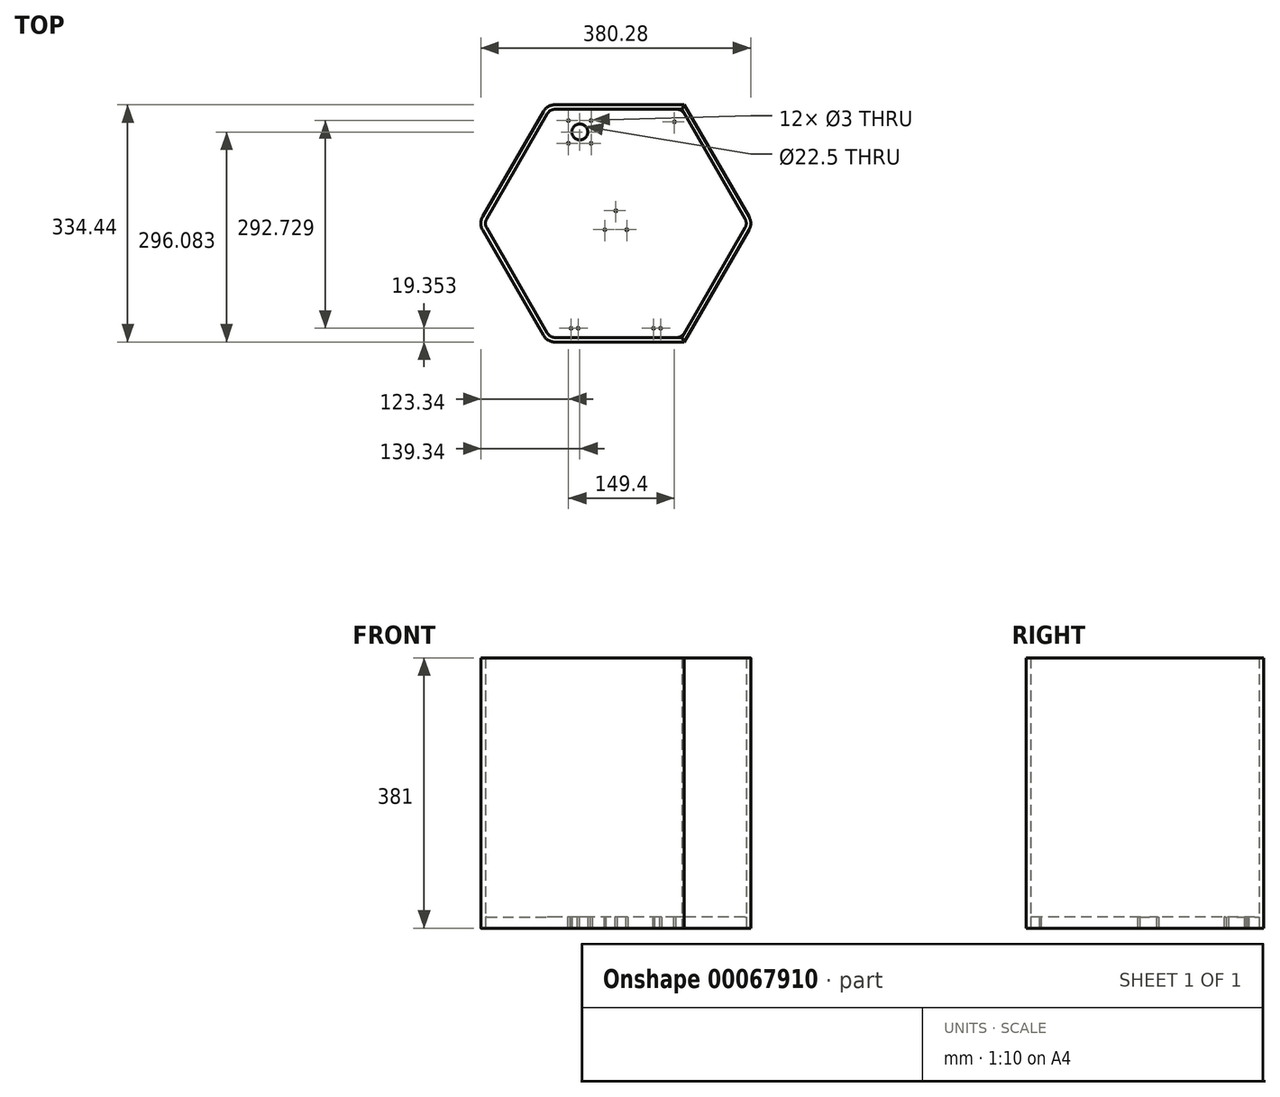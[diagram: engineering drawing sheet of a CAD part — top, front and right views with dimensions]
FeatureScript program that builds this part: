
annotation { "Feature Type Name" : "Feature", "Feature Type Description" : "" }
export const myFeature = defineFeature(function(context is Context, id is Id, definition is map)
    precondition{}
    {
        {
            var Q0;
            Q0=qCreatedBy(makeId("Top.planeOp"),FACE);
            var sketch = newSketch(context, id + "F0", { "sketchPlane" : qUnion([Q0])});
            skCircle(sketch, "E0.cCircle", {"center": v(0, 0) * mm, "radius": 160.87 * mm, "construction": true});
            skLineSegment(sketch, "E0.0", {"start": v(92.88, 160.87) * mm, "end": v(185.75, 0) * mm});
            skLineSegment(sketch, "E0.1", {"start": v(92.88, -160.87) * mm, "end": v(-92.88, -160.87) * mm});
            skLineSegment(sketch, "E0.2", {"start": v(-185.75, 0) * mm, "end": v(-92.88, 160.87) * mm});
            skPoint(sketch, "E0.0.midPoint", {"position": v(139.31, 80.43) * mm});
            skLineSegment(sketch, "E1.0", {"start": v(185.75, 0) * mm, "end": v(92.88, -160.87) * mm});
            skLineSegment(sketch, "E1.1", {"start": v(-92.88, -160.87) * mm, "end": v(-185.75, 0) * mm});
            skLineSegment(sketch, "E1.2", {"start": v(-92.88, 160.87) * mm, "end": v(92.88, 160.87) * mm});
            skPoint(sketch, "E1.0.midPoint", {"position": v(139.31, -80.43) * mm});
            skPoint(sketch, "E2.orphan", {"position": v(0, -321.73) * mm});
            skPoint(sketch, "E3.orphan", {"position": v(278.63, -160.87) * mm});
            skPoint(sketch, "E4.orphan", {"position": v(278.63, 160.87) * mm});
            skPoint(sketch, "E5.orphan", {"position": v(-278.63, 160.87) * mm});
            skPoint(sketch, "E6.orphan", {"position": v(-278.63, -160.87) * mm});
            skPoint(sketch, "E7.orphan", {"position": v(0, 321.73) * mm});
            skSolve(sketch);
        }
        {
            var Q0;
            Q0=makeQuery(id+"F0.imprint","IMPRINT",FACE,{"disambiguationData":[TD([[makeQuery(id+"F0.imprint","IMPRINT",EDGE,{"derivedFrom":sQuery(id+"F0.wireOp",EDGE,"E0.0")}),-1.0]])]});
            extrude(context, id + "F1", {"entities" : qUnion([Q0]), "depth" : 15.88 * mm});
        }
        {
            var Q0;
            Q0=makeQuery(id+"F1.opExtrude","SWEPT_EDGE",EDGE,{"disambiguationData":[OSD([sQuery(id+"F0.wireOp",EDGE,"E0.1"),sQuery(id+"F0.wireOp",EDGE,"E0.2")])]});
            var Q1;
            Q1=makeQuery(id+"F1.opExtrude","SWEPT_EDGE",EDGE,{"disambiguationData":[OSD([sQuery(id+"F0.wireOp",EDGE,"E0.0"),sQuery(id+"F0.wireOp",EDGE,"E0.1")])]});
            var Q2;
            Q2=makeQuery(id+"F1.opExtrude","SWEPT_EDGE",EDGE,{"disambiguationData":[OSD([sQuery(id+"F0.wireOp",EDGE,"E0.0"),sQuery(id+"F0.wireOp",EDGE,"E0.2")])]});
            fillet(context, id + "F2", {"entities" : qUnion([Q0, Q1, Q2]), "radius" : 12.7 * mm, "tangentPropagation" : true, "allowEdgeOverflow" : false});
        }
        {
            var Q0;
            Q0=qCreatedBy(makeId("Top.planeOp"),FACE);
            var sketch = newSketch(context, id + "F3", { "sketchPlane" : qUnion([Q0])});
            skPoint(sketch, "E8", {"position": v(-63.1, -147.87) * mm});
            skPoint(sketch, "E9", {"position": v(-53.1, -147.87) * mm});
            skPoint(sketch, "E10", {"position": v(53.1, -147.87) * mm});
            skPoint(sketch, "E11", {"position": v(63.1, -147.87) * mm});
            skSolve(sketch);
        }
        {
            var Q0;
            Q0=sQuery(id+"F3.wireOp",VERTEX,"E8");
            var Q1;
            Q1=sQuery(id+"F3.wireOp",VERTEX,"E9");
            var Q2;
            Q2=sQuery(id+"F3.wireOp",VERTEX,"E10");
            var Q3;
            Q3=sQuery(id+"F3.wireOp",VERTEX,"E11");
            var Q4;
            Q4=makeQuery(id+"F1.opExtrude","SWEPT_BODY",BODY,{"disambiguationData":[OSD([sQuery(id+"F0.wireOp",EDGE,"E0.0"),sQuery(id+"F0.wireOp",EDGE,"E0.1"),sQuery(id+"F0.wireOp",EDGE,"E0.2")])]});
            hole(context, id + "F4", {"style" : HoleStyle.SIMPLE, "endStyle" : HoleEndStyle.THROUGH, "oppositeDirection" : true, "holeDiameter" : 3 * mm, "locations" : qUnion([Q0, Q1, Q2, Q3]), "scope" : qUnion([Q4]), "isTappedThrough" : true});
        }
        {
            var Q0;
            Q0=qCreatedBy(makeId("Front.planeOp"),FACE);
            var sketch = newSketch(context, id + "F5", { "sketchPlane" : qUnion([Q0])});
            skLineSegment(sketch, "E12", {"start": v(0, 0) * mm, "end": v(0, 55.48) * mm});
            skSolve(sketch);
        }
        {
            var Q0;
            Q0=qCreatedBy(makeId("Top.planeOp"),FACE);
            var sketch = newSketch(context, id + "F6", { "sketchPlane" : qUnion([Q0])});
            skCircle(sketch, "E13.cCircle", {"center": v(0, 0) * mm, "radius": 8.89 * mm, "construction": true});
            skLineSegment(sketch, "E13.0", {"start": v(0, 17.78) * mm, "end": v(15.4, -8.9) * mm});
            skLineSegment(sketch, "E13.1", {"start": v(15.4, -8.9) * mm, "end": v(-15.4, -8.9) * mm});
            skLineSegment(sketch, "E13.2", {"start": v(-15.4, -8.89) * mm, "end": v(0, 17.78) * mm});
            skPoint(sketch, "E13.0.midPoint", {"position": v(7.7, 4.44) * mm});
            skSolve(sketch);
        }
        {
            var Q0;
            Q0=sQuery(id+"F6.wireOp",VERTEX,"E13.2.end");
            var Q1;
            Q1=sQuery(id+"F6.wireOp",VERTEX,"E13.1.end");
            var Q2;
            Q2=sQuery(id+"F6.wireOp",VERTEX,"E13.0.end");
            var Q3;
            Q3=makeQuery(id+"F1.opExtrude","SWEPT_BODY",BODY,{"disambiguationData":[OSD([sQuery(id+"F0.wireOp",EDGE,"E0.0"),sQuery(id+"F0.wireOp",EDGE,"E0.1"),sQuery(id+"F0.wireOp",EDGE,"E0.2")])]});
            hole(context, id + "F7", {"style" : HoleStyle.SIMPLE, "endStyle" : HoleEndStyle.THROUGH, "oppositeDirection" : true, "holeDiameter" : 3 * mm, "locations" : qUnion([Q0, Q1, Q2]), "scope" : qUnion([Q3]), "isTappedThrough" : true});
        }
        {
            var Q0;
            Q0=makeQuery(id+"F1.opExtrude","CAP_FACE",FACE,{"disambiguationData":[OSD([sQuery(id+"F0.wireOp",EDGE,"E0.0"),sQuery(id+"F0.wireOp",EDGE,"E0.1"),sQuery(id+"F0.wireOp",EDGE,"E0.2"),sQuery(id+"F0.wireOp",EDGE,"E1.0"),sQuery(id+"F0.wireOp",EDGE,"E1.1"),sQuery(id+"F0.wireOp",EDGE,"E1.2")])],"isStart":true});
            var sketch = newSketch(context, id + "F8", { "sketchPlane" : qUnion([Q0])});
            skLineSegment(sketch, "E14.bottom", {"start": v(-34.8, -112.86) * mm, "end": v(-66.8, -112.86) * mm});
            skLineSegment(sketch, "E14.top", {"start": v(-34.8, -144.86) * mm, "end": v(-66.8, -144.86) * mm});
            skLineSegment(sketch, "E14.left", {"start": v(-34.8, -112.86) * mm, "end": v(-34.8, -144.86) * mm});
            skLineSegment(sketch, "E14.right", {"start": v(-66.8, -112.86) * mm, "end": v(-66.8, -144.86) * mm});
            skPoint(sketch, "E14.middle", {"position": v(-50.8, -128.86) * mm});
            skSolve(sketch);
        }
        {
            var Q0;
            Q0=sQuery(id+"F8.wireOp",VERTEX,"E14.right.start");
            var Q1;
            Q1=sQuery(id+"F8.wireOp",VERTEX,"E14.left.start");
            var Q2;
            Q2=sQuery(id+"F8.wireOp",VERTEX,"E14.left.end");
            var Q3;
            Q3=sQuery(id+"F8.wireOp",VERTEX,"E14.top.end");
            var Q4;
            Q4=makeQuery(id+"F1.opExtrude","SWEPT_BODY",BODY,{"disambiguationData":[OSD([sQuery(id+"F0.wireOp",EDGE,"E0.0"),sQuery(id+"F0.wireOp",EDGE,"E0.1"),sQuery(id+"F0.wireOp",EDGE,"E0.2"),sQuery(id+"F0.wireOp",EDGE,"E1.0"),sQuery(id+"F0.wireOp",EDGE,"E1.1"),sQuery(id+"F0.wireOp",EDGE,"E1.2")])]});
            hole(context, id + "F9", {"style" : HoleStyle.SIMPLE, "endStyle" : HoleEndStyle.THROUGH, "holeDiameter" : 3 * mm, "locations" : qUnion([Q0, Q1, Q2, Q3]), "scope" : qUnion([Q4]), "isTappedThrough" : true});
        }
        {
            var Q0;
            Q0=sQuery(id+"F8.wireOp",VERTEX,"E14.middle");
            var Q1;
            Q1=makeQuery(id+"F1.opExtrude","SWEPT_BODY",BODY,{"disambiguationData":[OSD([sQuery(id+"F0.wireOp",EDGE,"E0.0"),sQuery(id+"F0.wireOp",EDGE,"E0.1"),sQuery(id+"F0.wireOp",EDGE,"E0.2"),sQuery(id+"F0.wireOp",EDGE,"E1.0"),sQuery(id+"F0.wireOp",EDGE,"E1.1"),sQuery(id+"F0.wireOp",EDGE,"E1.2")])]});
            hole(context, id + "F10", {"style" : HoleStyle.SIMPLE, "endStyle" : HoleEndStyle.THROUGH, "holeDiameter" : 22.5 * mm, "locations" : qUnion([Q0]), "scope" : qUnion([Q1]), "isTappedThrough" : true});
        }
        {
            var Q0;
            Q0=makeQuery(id+"F1.opExtrude","CAP_FACE",FACE,{"disambiguationData":[OSD([sQuery(id+"F0.wireOp",EDGE,"E0.0"),sQuery(id+"F0.wireOp",EDGE,"E0.1"),sQuery(id+"F0.wireOp",EDGE,"E0.2"),sQuery(id+"F0.wireOp",EDGE,"E1.0"),sQuery(id+"F0.wireOp",EDGE,"E1.1"),sQuery(id+"F0.wireOp",EDGE,"E1.2")])],"isStart":true});
            var sketch = newSketch(context, id + "F11", { "sketchPlane" : qUnion([Q0])});
            skLineSegment(sketch, "E15", {"start": v(109.77, -96) * mm, "end": v(68.07, -168.24) * mm, "construction": true});
            skLineSegment(sketch, "E16", {"start": v(12.41, -143.07) * mm, "end": v(92.71, -143.07) * mm, "construction": true});
            skPoint(sketch, "E17", {"position": v(82.6, -143.07) * mm});
            skSolve(sketch);
        }
        {
            var Q0;
            Q0=sQuery(id+"F11.wireOp",VERTEX,"E17");
            var Q1;
            Q1=makeQuery(id+"F1.opExtrude","SWEPT_BODY",BODY,{"disambiguationData":[OSD([sQuery(id+"F0.wireOp",EDGE,"E0.0"),sQuery(id+"F0.wireOp",EDGE,"E0.1"),sQuery(id+"F0.wireOp",EDGE,"E0.2"),sQuery(id+"F0.wireOp",EDGE,"E1.0"),sQuery(id+"F0.wireOp",EDGE,"E1.1"),sQuery(id+"F0.wireOp",EDGE,"E1.2")])]});
            hole(context, id + "F12", {"style" : HoleStyle.SIMPLE, "endStyle" : HoleEndStyle.THROUGH, "holeDiameter" : 3 * mm, "locations" : qUnion([Q0]), "scope" : qUnion([Q1]), "isTappedThrough" : true});
        }
        {
            var Q0;
            Q0=makeQuery(id+"F1.opExtrude","CAP_FACE",FACE,{"disambiguationData":[OSD([sQuery(id+"F0.wireOp",EDGE,"E0.0"),sQuery(id+"F0.wireOp",EDGE,"E0.1"),sQuery(id+"F0.wireOp",EDGE,"E0.2"),sQuery(id+"F0.wireOp",EDGE,"E1.0"),sQuery(id+"F0.wireOp",EDGE,"E1.1"),sQuery(id+"F0.wireOp",EDGE,"E1.2")])],"isStart":true});
            var sketch = newSketch(context, id + "F13", { "sketchPlane" : qUnion([Q0])});
            skLineSegment(sketch, "E18.0", {"start": v(-85.54, -160.87) * mm, "end": v(92.88, -160.87) * mm});
            skArc(sketch, "E18.1", {"start": v(-85.54, -160.87) * mm, "mid": v(-91.9, -159.17) * mm, "end": v(-96.54, -154.52) * mm});
            skLineSegment(sketch, "E18.2", {"start": v(-182.09, -6.35) * mm, "end": v(-96.54, -154.52) * mm});
            skArc(sketch, "E18.3", {"start": v(-182.09, -6.35) * mm, "mid": v(-183.79, 0) * mm, "end": v(-182.09, 6.35) * mm});
            skLineSegment(sketch, "E18.4", {"start": v(-96.54, 154.52) * mm, "end": v(-182.09, 6.35) * mm});
            skArc(sketch, "E18.5", {"start": v(-96.54, 154.52) * mm, "mid": v(-91.9, 159.17) * mm, "end": v(-85.54, 160.87) * mm});
            skLineSegment(sketch, "E18.6", {"start": v(92.88, 160.87) * mm, "end": v(-85.54, 160.87) * mm});
            skLineSegment(sketch, "E19.0", {"start": v(-85.54, -167.22) * mm, "end": v(96.54, -167.22) * mm});
            skArc(sketch, "E19.1", {"start": v(-85.54, -167.22) * mm, "mid": v(-95.07, -164.66) * mm, "end": v(-102.04, -157.7) * mm});
            skLineSegment(sketch, "E19.2", {"start": v(-187.59, -9.52) * mm, "end": v(-102.04, -157.7) * mm});
            skLineSegment(sketch, "E19.3", {"start": v(96.54, 167.22) * mm, "end": v(-85.54, 167.22) * mm});
            skArc(sketch, "E19.4", {"start": v(-102.04, 157.7) * mm, "mid": v(-95.07, 164.66) * mm, "end": v(-85.54, 167.22) * mm});
            skLineSegment(sketch, "E19.5", {"start": v(-102.04, 157.7) * mm, "end": v(-187.59, 9.53) * mm});
            skArc(sketch, "E19.6", {"start": v(-187.59, -9.52) * mm, "mid": v(-190.14, 0) * mm, "end": v(-187.59, 9.53) * mm});
            skLineSegment(sketch, "E20", {"start": v(96.54, -167.22) * mm, "end": v(92.88, -160.87) * mm});
            skPoint(sketch, "E21.orphan", {"position": v(85.54, -160.87) * mm});
            skLineSegment(sketch, "E22", {"start": v(96.54, 167.22) * mm, "end": v(76.1, 131.81) * mm});
            skPoint(sketch, "E23.orphan", {"position": v(85.54, 160.87) * mm});
            skSolve(sketch);
        }
        {
            var Q0;
            Q0 = qSketchRegion(id + "F13", true);
            extrude(context, id + "F14", {"entities" : qUnion([Q0]), "oppositeDirection" : true, "depth" : 381 * mm});
        }
        {
            var Q0;
            Q0=makeQuery(id+"F1.opExtrude","CAP_FACE",FACE,{"disambiguationData":[OSD([sQuery(id+"F0.wireOp",EDGE,"E0.0"),sQuery(id+"F0.wireOp",EDGE,"E0.1"),sQuery(id+"F0.wireOp",EDGE,"E0.2"),sQuery(id+"F0.wireOp",EDGE,"E1.0"),sQuery(id+"F0.wireOp",EDGE,"E1.1"),sQuery(id+"F0.wireOp",EDGE,"E1.2")])],"isStart":true});
            var sketch = newSketch(context, id + "F15", { "sketchPlane" : qUnion([Q0])});
            skLineSegment(sketch, "E24.0", {"start": v(182.09, 6.35) * mm, "end": v(92.88, 160.87) * mm});
            skArc(sketch, "E24.1", {"start": v(182.09, -6.35) * mm, "mid": v(183.79, 0) * mm, "end": v(182.09, 6.35) * mm});
            skLineSegment(sketch, "E24.2", {"start": v(92.88, -160.87) * mm, "end": v(182.09, -6.35) * mm});
            skLineSegment(sketch, "E25.0", {"start": v(187.59, 9.53) * mm, "end": v(96.54, 167.22) * mm});
            skArc(sketch, "E25.1", {"start": v(187.59, -9.52) * mm, "mid": v(190.14, 0) * mm, "end": v(187.59, 9.53) * mm});
            skLineSegment(sketch, "E25.2", {"start": v(96.54, -167.22) * mm, "end": v(187.59, -9.52) * mm});
            skLineSegment(sketch, "E26", {"start": v(92.88, -160.87) * mm, "end": v(96.54, -167.22) * mm});
            skPoint(sketch, "E27.orphan", {"position": v(91.9, -159.17) * mm});
            skPoint(sketch, "E28.orphan", {"position": v(96.54, -154.52) * mm});
            skPoint(sketch, "E29.orphan", {"position": v(96.54, 154.52) * mm});
            skLineSegment(sketch, "E30", {"start": v(92.88, 160.87) * mm, "end": v(96.54, 167.22) * mm});
            skSolve(sketch);
        }
        {
            var Q0;
            Q0 = qSketchRegion(id + "F15", true);
            extrude(context, id + "F16", {"entities" : qUnion([Q0]), "oppositeDirection" : true, "depth" : 381 * mm});
        }
    });
